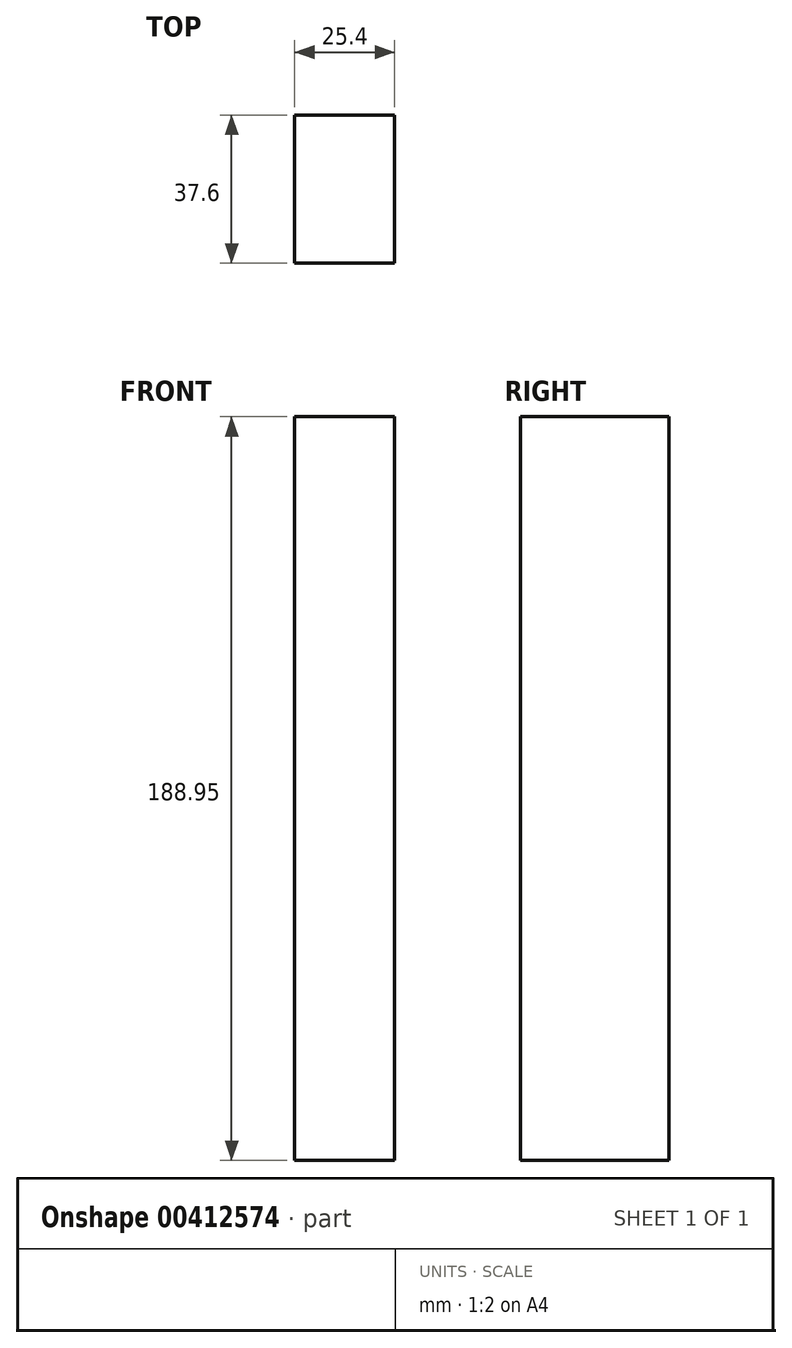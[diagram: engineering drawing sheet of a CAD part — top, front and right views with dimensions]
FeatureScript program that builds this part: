
annotation { "Feature Type Name" : "Feature", "Feature Type Description" : "" }
export const myFeature = defineFeature(function(context is Context, id is Id, definition is map)
    precondition{}
    {
        {
            var Q0;
            Q0=qCreatedBy(makeId("Right.planeOp"),FACE);
            var sketch = newSketch(context, id + "F0", { "sketchPlane" : qUnion([Q0])});
            skLineSegment(sketch, "E0.bottom", {"start": v(91.08, 92.71) * mm, "end": v(53.48, 92.71) * mm});
            skLineSegment(sketch, "E0.top", {"start": v(91.08, -96.24) * mm, "end": v(53.48, -96.24) * mm});
            skLineSegment(sketch, "E0.left", {"start": v(91.08, 92.71) * mm, "end": v(91.08, -96.24) * mm});
            skLineSegment(sketch, "E0.right", {"start": v(53.48, 92.71) * mm, "end": v(53.48, -96.24) * mm});
            skLineSegment(sketch, "E1.bottom", {"start": v(53.48, 92.71) * mm, "end": v(53.48, 92.71) * mm});
            skLineSegment(sketch, "E1.top", {"start": v(53.48, 92.71) * mm, "end": v(53.48, 92.71) * mm});
            skLineSegment(sketch, "E1.left", {"start": v(53.48, 92.71) * mm, "end": v(53.48, 92.71) * mm});
            skLineSegment(sketch, "E1.right", {"start": v(53.48, 92.71) * mm, "end": v(53.48, 92.71) * mm});
            skSolve(sketch);
        }
        {
            var Q0;
            Q0=makeQuery(id+"F0.imprint","IMPRINT",FACE,{"disambiguationData":[TD([[makeQuery(id+"F0.imprint","IMPRINT",EDGE,{"derivedFrom":sQuery(id+"F0.wireOp",EDGE,"E0.bottom")}),1.0]])]});
            extrude(context, id + "F1", {"entities" : qUnion([Q0]), "depth" : 25.4 * mm});
        }
    });
